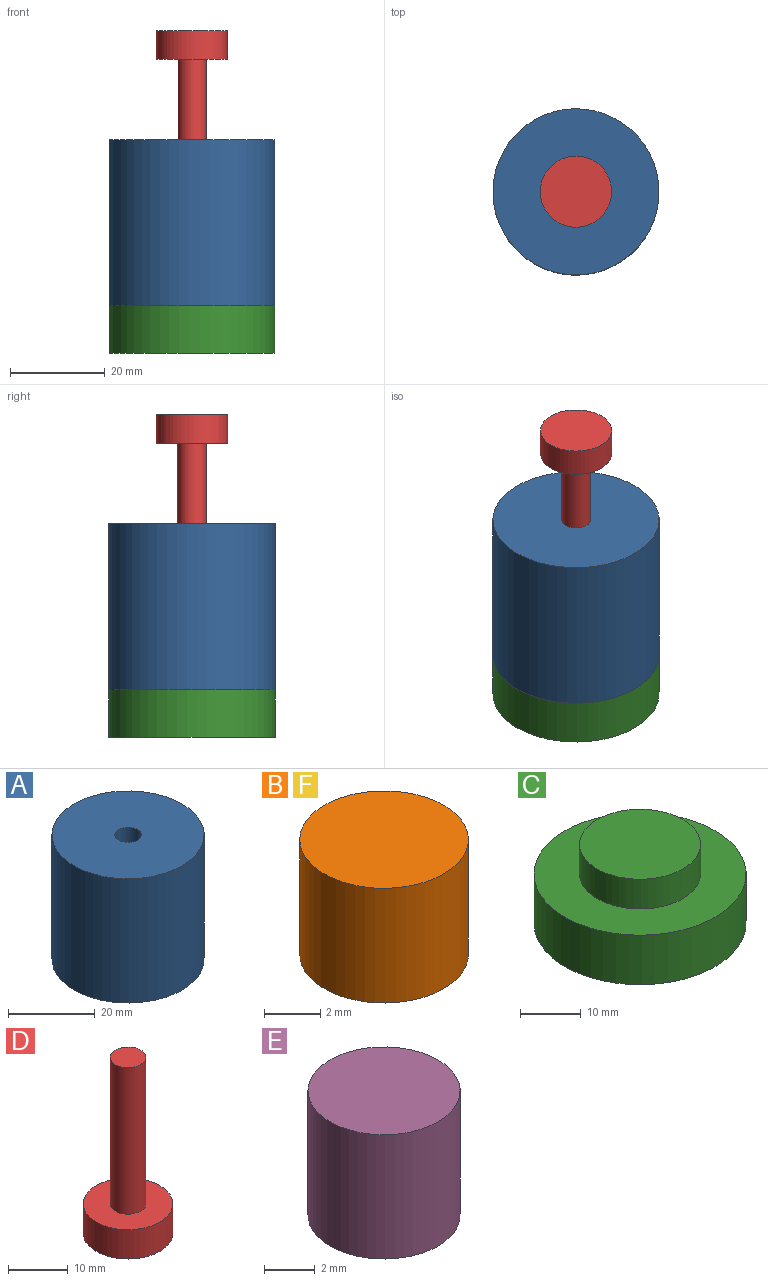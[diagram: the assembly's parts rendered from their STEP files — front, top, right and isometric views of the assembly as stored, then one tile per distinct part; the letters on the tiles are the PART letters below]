
ASSEMBLY  parts=6 mates=10
PART A: 6 faces, bbox 35x35x35 mm
  f0: cylinder r=3.03mm len=29mm, axis (0,0,1), area 551.6mm2, adj f3,f5
  f1: cylinder r=17.5mm len=35mm, axis (0,0,1), area 3848.5mm2, adj f2,f3
  f2: plane 35x35mm, normal (0,0,-1), area 632mm2, adj f1,f4
  f3: plane 35x35mm, normal (0,0,1), area 933.3mm2, adj f0,f1
  f4: cylinder r=10.25mm len=20.5mm, axis (0,0,-1), area 386.4mm2, adj f2,f5
  f5: plane 20.5x20.5mm, normal (0,0,-1), area 301.3mm2, adj f0,f4
PART B: 3 faces, bbox 6x6x5 mm
  f0: cylinder r=3mm len=6mm, axis (0,0,-1), area 94.2mm2, adj f1,f2
  f1: plane 6x6mm, normal (0,0,1), area 28.3mm2, adj f0
  f2: plane 6x6mm, normal (0,0,-1), area 28.3mm2, adj f0
PART C: 5 faces, bbox 35x35x16 mm
  f0: cylinder r=17.5mm len=35mm, axis (0,0,-1), area 1099.6mm2, adj f1,f3
  f1: plane 35x35mm, normal (0,0,-1), area 962.1mm2, adj f0
  f2: cylinder r=10mm len=20mm, axis (0,0,1), area 377mm2, adj f3,f4
  f3: plane 35x35mm, normal (0,0,1), area 648mm2, adj f0,f2
  f4: plane 20x20mm, normal (0,0,1), area 314.2mm2, adj f2
PART D: 5 faces, bbox 15x15x36 mm
  f0: cylinder r=7.5mm len=15mm, axis (0,0,1), area 282.7mm2, adj f1,f2
  f1: plane 15x15mm, normal (0,0,-1), area 176.7mm2, adj f0
  f2: plane 15x15mm, normal (0,0,1), area 148.4mm2, adj f0,f3
  f3: cylinder r=3mm len=30mm, axis (0,0,-1), area 565.5mm2, adj f2,f4
  f4: plane 6x6mm, normal (0,0,1), area 28.3mm2, adj f3
PART E: 3 faces, bbox 6x6x6 mm
  f0: cylinder r=3mm len=6mm, axis (0,0,-1), area 113.1mm2, adj f1,f2
  f1: plane 6x6mm, normal (0,0,1), area 28.3mm2, adj f0
  f2: plane 6x6mm, normal (0,0,-1), area 28.3mm2, adj f0
PART F: same geometry as B
PLACE A t=(11.57,6.41,23.43)mm
PLACE B t=(11.57,6.41,5.43)mm
PLACE C t=(11.57,6.41,-21.57)mm
PLACE D rot(axis=(1,0,0),180deg) t=(11.57,6.41,40.43)mm
PLACE E t=(11.57,6.41,-0.57)mm
PLACE F t=(11.57,6.41,-5.57)mm
MATE planar C.f0 <-> A.f1  axis (0,0,1) through (11.57,6.41,-11.57)mm
MATE planar D.f3 <-> B.f0  axis (0,0,-1) through (11.57,6.41,10.43)mm
MATE planar E.f0 <-> F.f0  axis (0,0,-1) through (11.57,6.41,-0.57)mm
MATE slider D.f3 <-> A.f1  axis (0,0,1) through (11.57,6.41,25.43)mm
MATE slider F.f0 <-> A.f0  axis (0,0,-1) through (11.57,6.41,-3.07)mm
MATE planar E.f0 <-> B.f0  axis (0,0,1) through (11.57,6.41,5.43)mm
MATE slider B.f0 <-> A.f0  axis (0,0,-1) through (11.57,6.41,7.93)mm
MATE planar F.f0 <-> C.f2  axis (0,0,-1) through (11.57,6.41,-5.57)mm
MATE slider C.f0 <-> A.f4  axis (0,0,-1) through (11.57,6.41,-21.57)mm
MATE slider E.f0 <-> A.f0  axis (0,0,1) through (11.57,6.41,5.43)mm
